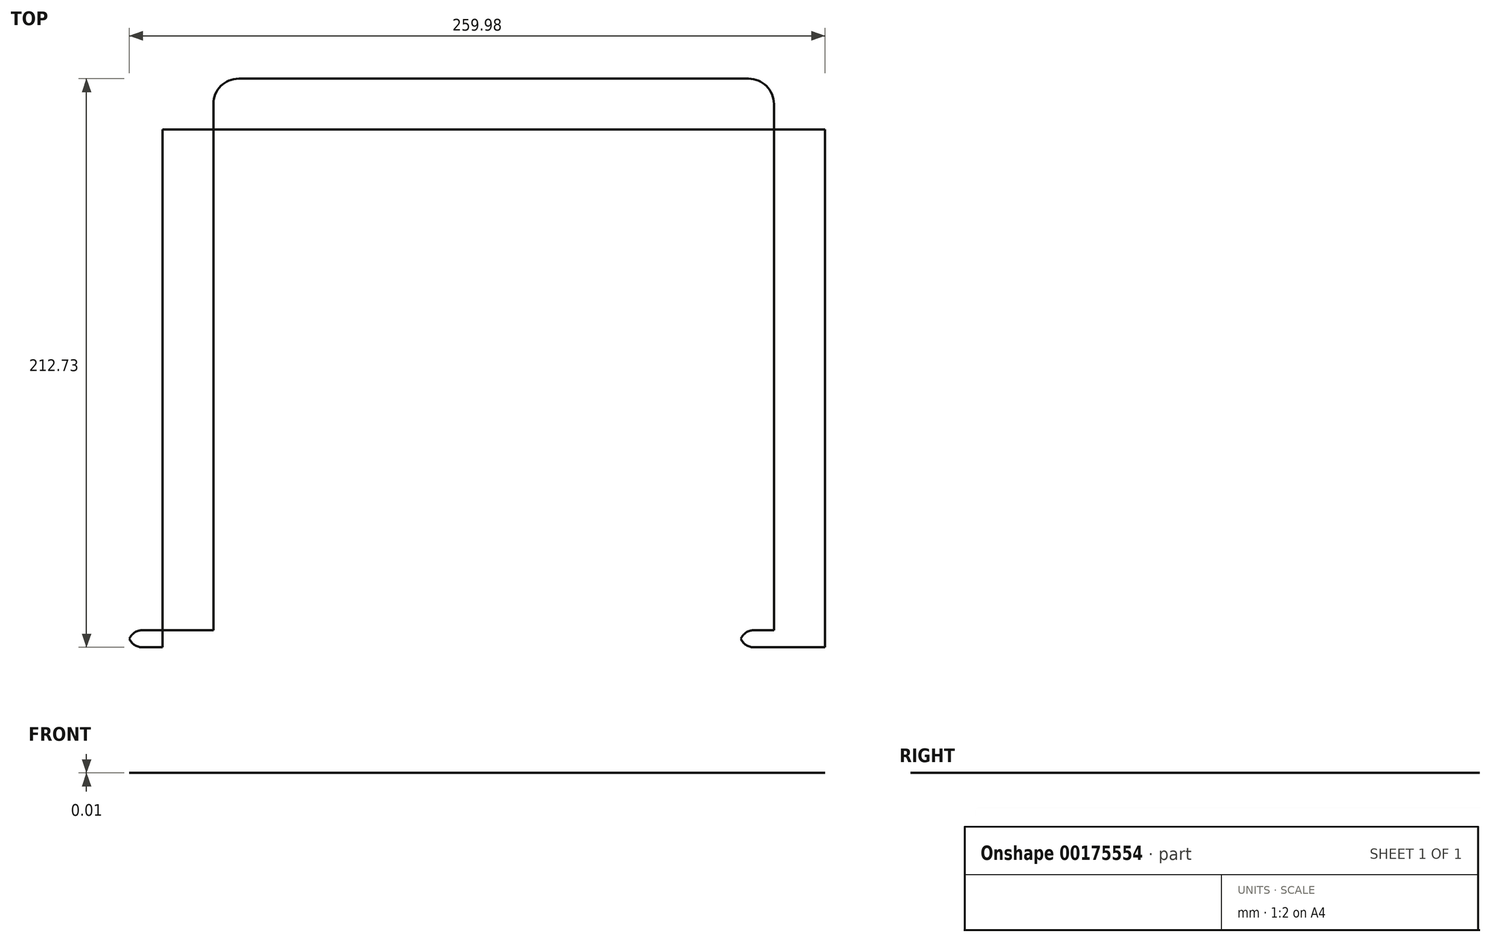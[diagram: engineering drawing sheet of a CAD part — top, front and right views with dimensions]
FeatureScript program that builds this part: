
annotation { "Feature Type Name" : "Feature", "Feature Type Description" : "" }
export const myFeature = defineFeature(function(context is Context, id is Id, definition is map)
    precondition{}
    {
        {
            var Q0;
            Q0=qCreatedBy(makeId("Top.planeOp"),FACE);
            var sketch = newSketch(context, id + "F0", { "sketchPlane" : qUnion([Q0])});
            skLineSegment(sketch, "E0.bottom", {"start": v(-247.65, 19.05) * mm, "end": v(-228.6, 19.05) * mm});
            skLineSegment(sketch, "E0.top", {"start": v(-247.65, -193.68) * mm, "end": v(-228.6, -193.68) * mm});
            skLineSegment(sketch, "E0.left", {"start": v(-247.65, 19.05) * mm, "end": v(-247.65, -193.68) * mm});
            skLineSegment(sketch, "E0.right", {"start": v(-228.6, 19.05) * mm, "end": v(-228.6, -193.68) * mm});
            skLineSegment(sketch, "E1.bottom", {"start": v(-19.05, 19.05) * mm, "end": v(0, 19.05) * mm});
            skLineSegment(sketch, "E1.top", {"start": v(-19.05, -193.68) * mm, "end": v(0, -193.68) * mm});
            skLineSegment(sketch, "E1.left", {"start": v(-19.05, 19.05) * mm, "end": v(-19.05, -193.68) * mm});
            skLineSegment(sketch, "E1.right", {"start": v(0, 19.05) * mm, "end": v(0, -193.68) * mm});
            skLineSegment(sketch, "E2.bottom", {"start": v(-31.75, -187.33) * mm, "end": v(0, -187.33) * mm});
            skLineSegment(sketch, "E2.top", {"start": v(-31.75, -193.68) * mm, "end": v(0, -193.68) * mm});
            skLineSegment(sketch, "E2.left", {"start": v(-31.75, -187.33) * mm, "end": v(-31.75, -193.68) * mm});
            skLineSegment(sketch, "E2.right", {"start": v(0, -187.33) * mm, "end": v(0, -193.68) * mm});
            skLineSegment(sketch, "E3.bottom", {"start": v(-228.6, -193.68) * mm, "end": v(-260.35, -193.68) * mm});
            skLineSegment(sketch, "E3.top", {"start": v(-228.6, -187.33) * mm, "end": v(-260.35, -187.33) * mm});
            skLineSegment(sketch, "E3.left", {"start": v(-228.6, -193.68) * mm, "end": v(-228.6, -187.33) * mm});
            skLineSegment(sketch, "E3.right", {"start": v(-260.35, -193.68) * mm, "end": v(-260.35, -187.33) * mm});
            skLineSegment(sketch, "E4.bottom", {"start": v(-247.65, 19.05) * mm, "end": v(0, 19.05) * mm});
            skLineSegment(sketch, "E4.top", {"start": v(-247.65, 0) * mm, "end": v(0, 0) * mm});
            skLineSegment(sketch, "E4.left", {"start": v(-247.65, 19.05) * mm, "end": v(-247.65, 0) * mm});
            skLineSegment(sketch, "E4.right", {"start": v(0, 19.05) * mm, "end": v(0, 0) * mm});
            skCircle(sketch, "E5", {"center": v(-9.52, 9.53) * mm, "radius": 1.59 * mm});
            skPoint(sketch, "E5.centerSnap0", {"position": v(0, 9.53) * mm});
            skPoint(sketch, "E5.centerSnap1", {"position": v(-9.52, 19.05) * mm});
            skCircle(sketch, "E6", {"center": v(-238.13, 9.53) * mm, "radius": 1.59 * mm});
            skPoint(sketch, "E6.centerSnap0", {"position": v(-238.13, 19.05) * mm});
            skSolve(sketch);
        }
        {
            var Q0;
            {var subQ5=sQuery(id+"F0.wireOp",EDGE,"E3.right");Q0=makeQuery(id+"F0.imprint","IMPRINT",FACE,{"disambiguationData":[TD([[makeQuery(id+"F0.imprint","IMPRINT",EDGE,{"derivedFrom":subQ5}),-1.0]])]});}
            var Q1;
            {var subQ5=sQuery(id+"F0.wireOp",EDGE,"E3.left");Q1=makeQuery(id+"F0.imprint","IMPRINT",FACE,{"disambiguationData":[TD([[makeQuery(id+"F0.imprint","IMPRINT",EDGE,{"derivedFrom":subQ5}),1.0]])]});}
            var Q2;
            {var subQ1=sQuery(id+"F0.wireOp",EDGE,"E0.left");var subQ3=sQuery(id+"F0.wireOp",EDGE,"E3.top");var subQ4=makeQuery(id+"F0.imprint","INTERSECT",VERTEX,{"derivedFrom":[subQ1,subQ3]});Q2=makeQuery(id+"F0.imprint","IMPRINT",FACE,{"disambiguationData":[TD([[makeQuery(id+"F0.imprint","IMPRINT",EDGE,{"disambiguationData":[TD([[subQ4,1.0]])],"derivedFrom":subQ1}),1.0]])]});}
            var Q3;
            {var subQ0=sQuery(id+"F0.wireOp",EDGE,"E4.left");Q3=makeQuery(id+"F0.imprint","IMPRINT",FACE,{"disambiguationData":[TD([[makeQuery(id+"F0.imprint","IMPRINT",EDGE,{"derivedFrom":subQ0}),1.0]])]});}
            var Q4;
            {var subQ0=sQuery(id+"F0.wireOp",EDGE,"E4.bottom");var subQ1=sQuery(id+"F0.wireOp",EDGE,"E0.right");var subQ2=makeQuery(id+"F0.imprint","INTERSECT",VERTEX,{"derivedFrom":[subQ1,subQ0]});Q4=makeQuery(id+"F0.imprint","IMPRINT",FACE,{"disambiguationData":[TD([[makeQuery(id+"F0.imprint","IMPRINT",EDGE,{"disambiguationData":[TD([[subQ2,-1.0]])],"derivedFrom":subQ1}),1.0]])]});}
            var Q5;
            {var subQ0=sQuery(id+"F0.wireOp",EDGE,"E4.right");Q5=makeQuery(id+"F0.imprint","IMPRINT",FACE,{"disambiguationData":[TD([[makeQuery(id+"F0.imprint","IMPRINT",EDGE,{"derivedFrom":subQ0}),-1.0]])]});}
            var Q6;
            {var subQ5=sQuery(id+"F0.wireOp",EDGE,"E1.right");Q6=makeQuery(id+"F0.imprint","IMPRINT",FACE,{"disambiguationData":[TD([[makeQuery(id+"F0.imprint","IMPRINT",EDGE,{"derivedFrom":subQ5}),-1.0]])]});}
            var Q7;
            {var subQ5=sQuery(id+"F0.wireOp",EDGE,"E2.right");Q7=makeQuery(id+"F0.imprint","IMPRINT",FACE,{"disambiguationData":[TD([[makeQuery(id+"F0.imprint","IMPRINT",EDGE,{"derivedFrom":subQ5}),-1.0]])]});}
            var Q8;
            {var subQ5=sQuery(id+"F0.wireOp",EDGE,"E2.left");Q8=makeQuery(id+"F0.imprint","IMPRINT",FACE,{"disambiguationData":[TD([[makeQuery(id+"F0.imprint","IMPRINT",EDGE,{"derivedFrom":subQ5}),1.0]])]});}
            extrude(context, id + "F1", {"entities" : qUnion([Q0, Q1, Q2, Q3, Q4, Q5, Q6, Q7, Q8]), "depth" : 1 / 101.6 * mm});
        }
        {
            var Q0;
            Q0=makeQuery(id+"F1.opExtrude","SWEPT_EDGE",EDGE,{"disambiguationData":[OSD([sQuery(id+"F0.wireOp",EDGE,"E4.bottom"),sQuery(id+"F0.wireOp",EDGE,"E4.right")])]});
            var Q1;
            Q1=makeQuery(id+"F1.opExtrude","SWEPT_EDGE",EDGE,{"disambiguationData":[OSD([sQuery(id+"F0.wireOp",EDGE,"E4.bottom"),sQuery(id+"F0.wireOp",EDGE,"E4.left")])]});
            fillet(context, id + "F2", {"entities" : qUnion([Q0, Q1]), "radius" : 9.52 * mm, "tangentPropagation" : true, "allowEdgeOverflow" : false});
        }
        {
            var Q0;
            Q0=makeQuery(id+"F1.opExtrude","SWEPT_EDGE",EDGE,{"disambiguationData":[OSD([sQuery(id+"F0.wireOp",EDGE,"E3.top"),sQuery(id+"F0.wireOp",EDGE,"E3.right")])]});
            var Q1;
            Q1=makeQuery(id+"F1.opExtrude","SWEPT_EDGE",EDGE,{"disambiguationData":[OSD([sQuery(id+"F0.wireOp",EDGE,"E2.bottom"),sQuery(id+"F0.wireOp",EDGE,"E2.left")])]});
            var Q2;
            Q2=makeQuery(id+"F1.opExtrude","SWEPT_EDGE",EDGE,{"disambiguationData":[OSD([sQuery(id+"F0.wireOp",EDGE,"E3.bottom"),sQuery(id+"F0.wireOp",EDGE,"E3.right")])]});
            var Q3;
            Q3=makeQuery(id+"F1.opExtrude","SWEPT_EDGE",EDGE,{"disambiguationData":[OSD([sQuery(id+"F0.wireOp",EDGE,"E2.top"),sQuery(id+"F0.wireOp",EDGE,"E2.left")])]});
            fillet(context, id + "F3", {"entities" : qUnion([Q0, Q1, Q2, Q3]), "radius" : 5.08 * mm, "tangentPropagation" : true, "allowEdgeOverflow" : false});
        }
    });
